# Revit family: 0039314
name_source: partatom
category: Lighting Fixtures
revit_build: Autodesk Revit 2017 (Build: 20190507_1515(x64)
units: mm (PartAtom-declared; Revit-internal decimal feet)

## family parameters
Cut with Voids When Loaded = No
Host = Face
Light Source = Yes
OmniClass Number = 23.80.70.11.17
OmniClass Title = Specialized Lighting by Location or Use
Part Type = Normal
Room Calculation Point = No
Round Connector Dimension = Use Diameter
Shared = No

## types (1)
- START LED HIGHBAY 4000K 10KLM WIDE DALI
    Apparent Load = 95 VA
    Assembly Code = D5020200
    Beam Angle = 85°
    Catalog Number = 0039314 START LED HIGHBAY 4000K 10KLM WIDE DALI
    Color Filter = 16777215
    Default Elevation = 0 mm  [stored 0 ft]
    Description = The new Start LED Highbay is a range of industrial fixtures developed for retail, industry, manufacturing, airports and data centres. Start LED Highbay delivers high performance: up to 21,573 lm (luminaire lumen output on 190W version) and delivers up to 114 lm/W (total system efficiency). Start LED Highbay is available in 2 versions (95W or 190W) and 2 beam angles (medium or wide beam), allowing you to choose the best option depending the job on hand. Being part of the EVO LED range of luminaires means Start LED Highbay has been developed for efficiency, functionality and reliability; making it the go-to range for installers and contractors.
    Diameter = 280.4 mm  [stored 0.919948 ft]
    Diffuser Diameter = 220.4 mm
    Diffuser Material = Polycarbonate_Sylvania_Start LED HighBay_Clear
    Diffuser Radius = 110.2 mm
    Dimming Lamp Color Temperature Shift = <None>
    Drive Current = 2450 mA
    Electrical Protection = CLASS I
    Emit Shape Visible in Rendering = Yes
    Emit from Circle Diameter = 220.4 mm
    Energy Class = A++,A+,A
    Housing Material = Magnesium_Sylvania_Start LED HighBay_Silver_RAL 9006
    IK Rating = IK08
    IP Rating = IP65
    Lamp = LED Panel
    Life = 50 000 h
    Manufacturer = Feilo-Sylvania Group
    Model = START LED HIGHBAY 4000K 10KLM WIDE DALI
    Mounting Bracket Length = 30 mm  [stored 0.0984252 ft]
    Mounting Bracket Width = 100 mm  [stored 0.328084 ft]
    Mounting Brackets Distance = 94.7 mm
    Mounting Height = 1000 mm  [stored 3.28084 ft]
    Mounting Material = Metal_Sylvania_Start LED HighBay_Silver
    Mounting Radius = 50 mm
    Photometric Web File = 0039314_STARTLEDHIGHBAY4000K10KLMWIDEDALI-207910.ies
    Product Family = Start LED Highbay
    Product Page URL = https://www.sylvania-lighting.com
    Radius = 140.2 mm  [stored 0.459974 ft]
    Tilt Angle = -90°
    URL = https://www.sylvania-lighting.com
    Voltage = 230 V
    Voltage Comments = UNV (Universal Voltage; 220-240 Volt)
    Weight = 3 kg

note: [stored X ft] marks values corroborated as IEEE doubles in the binary element streams (Revit-internal decimal feet)

## geometry (parser evidence)
native form markers: Sweep x3
no freeform markers — native parametric forms only
